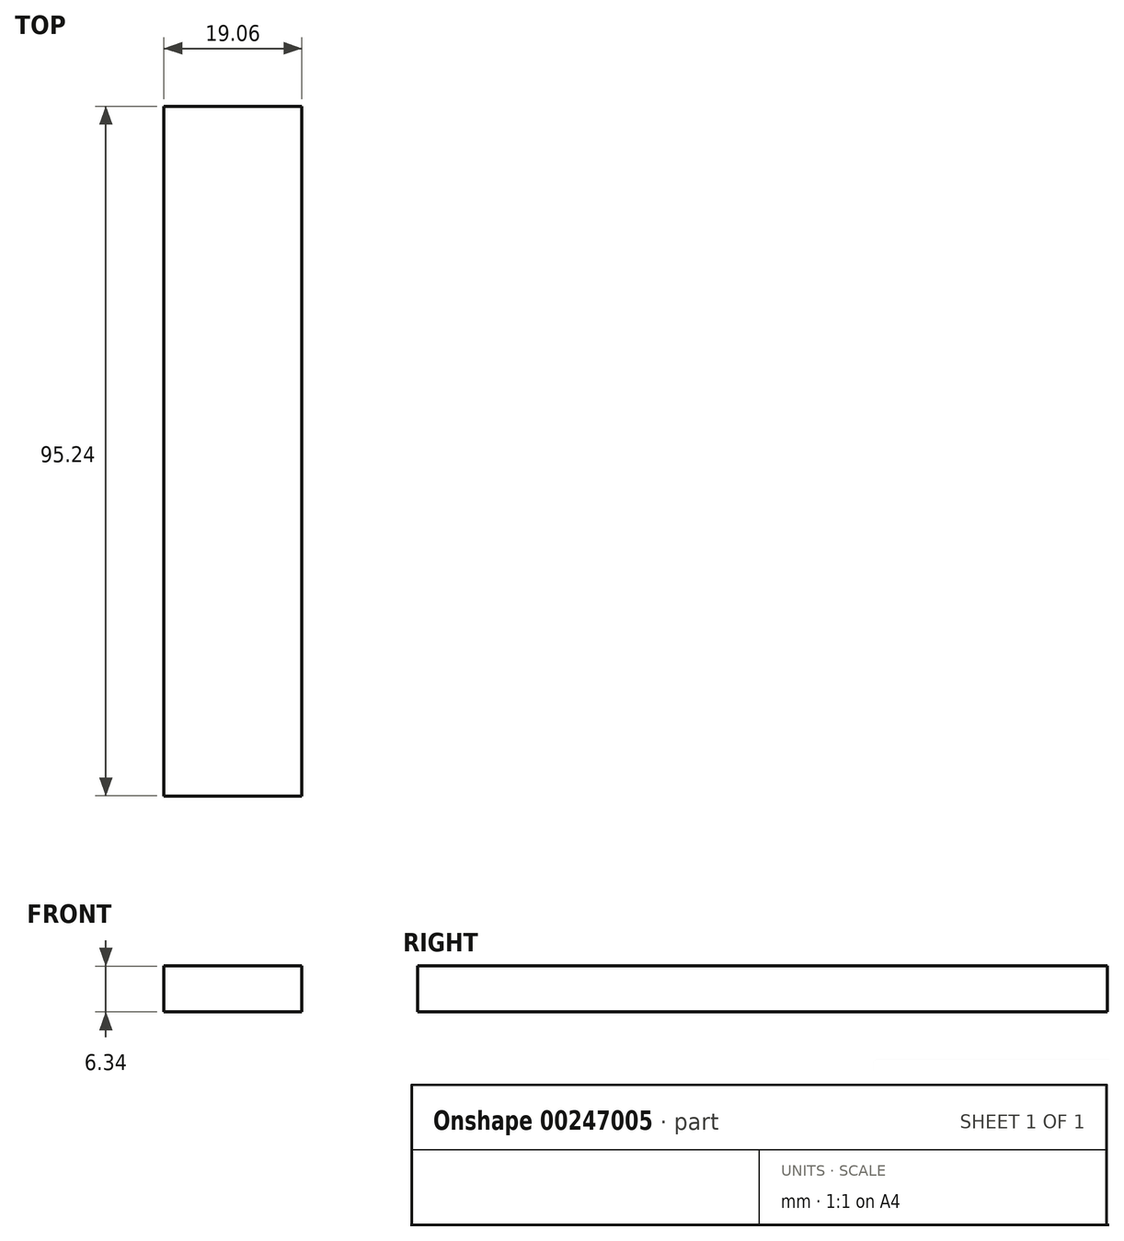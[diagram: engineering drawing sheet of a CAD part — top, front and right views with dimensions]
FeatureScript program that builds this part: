
annotation { "Feature Type Name" : "Feature", "Feature Type Description" : "" }
export const myFeature = defineFeature(function(context is Context, id is Id, definition is map)
    precondition{}
    {
        {
            var Q0;
            Q0=qCreatedBy(makeId("Front.planeOp"),FACE);
            var sketch = newSketch(context, id + "F0", { "sketchPlane" : qUnion([Q0])});
            skLineSegment(sketch, "E0.bottom", {"start": v(9.53, 3.17) * mm, "end": v(-9.53, 3.17) * mm});
            skLineSegment(sketch, "E0.top", {"start": v(9.53, -3.17) * mm, "end": v(-9.53, -3.17) * mm});
            skLineSegment(sketch, "E0.left", {"start": v(9.53, 3.17) * mm, "end": v(9.53, -3.17) * mm});
            skLineSegment(sketch, "E0.right", {"start": v(-9.53, 3.17) * mm, "end": v(-9.53, -3.17) * mm});
            skPoint(sketch, "E0.middle", {"position": v(0, 0) * mm});
            skSolve(sketch);
        }
        {
            var Q0;
            Q0 = qSketchRegion(id + "F0", true);
            extrude(context, id + "F1", {"entities" : qUnion([Q0]), "endBound" : BoundingType.SYMMETRIC, "depth" : 95.25 * mm});
        }
    });
